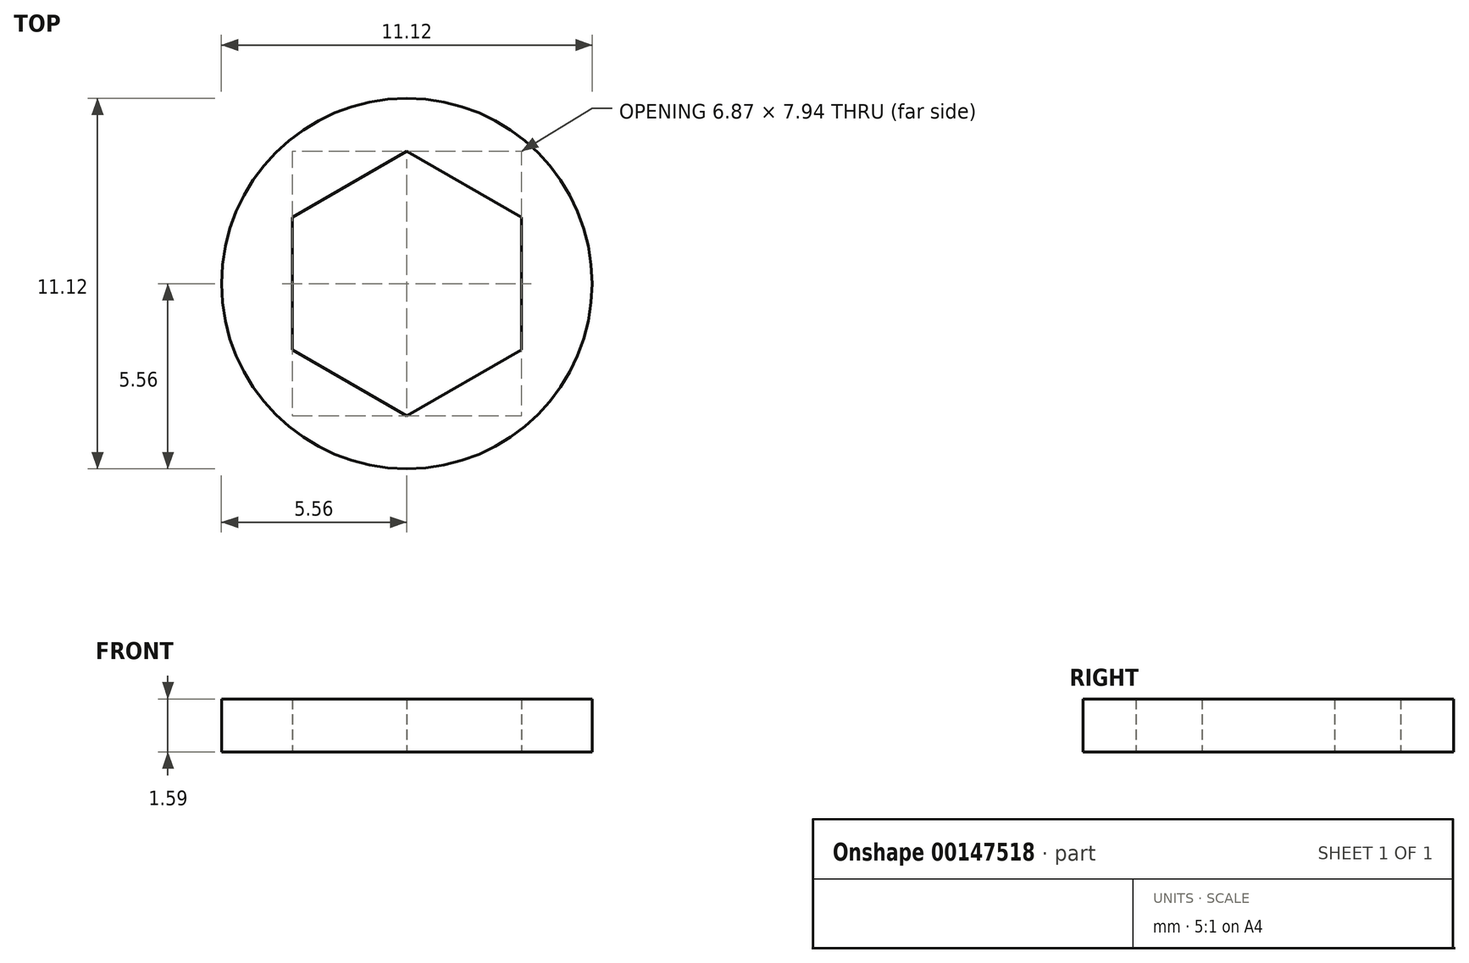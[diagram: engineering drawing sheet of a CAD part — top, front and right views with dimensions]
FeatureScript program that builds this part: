
annotation { "Feature Type Name" : "Feature", "Feature Type Description" : "" }
export const myFeature = defineFeature(function(context is Context, id is Id, definition is map)
    precondition{}
    {
        {
            var Q0;
            Q0=qCreatedBy(makeId("Top.planeOp"),FACE);
            var sketch = newSketch(context, id + "F0", { "sketchPlane" : qUnion([Q0])});
            skCircle(sketch, "E0.cCircle", {"center": v(0, 0) * mm, "radius": 3.97 * mm, "construction": true});
            skLineSegment(sketch, "E0.0", {"start": v(0, -3.97) * mm, "end": v(-3.44, -1.98) * mm});
            skLineSegment(sketch, "E0.1", {"start": v(-3.44, -1.98) * mm, "end": v(-3.44, 1.98) * mm});
            skLineSegment(sketch, "E0.2", {"start": v(-3.44, 1.98) * mm, "end": v(0, 3.97) * mm});
            skLineSegment(sketch, "E0.3", {"start": v(0, 3.97) * mm, "end": v(3.44, 1.98) * mm});
            skLineSegment(sketch, "E0.4", {"start": v(3.44, 1.98) * mm, "end": v(3.44, -1.98) * mm});
            skLineSegment(sketch, "E0.5", {"start": v(3.44, -1.98) * mm, "end": v(0, -3.97) * mm});
            skCircle(sketch, "E1", {"center": v(0, 0) * mm, "radius": 5.56 * mm});
            skSolve(sketch);
        }
        {
            var Q0;
            Q0=qSketchRegion(id+"F0",true);
            extrude(context, id + "F1", {"entities" : qUnion([Q0]), "depth" : 1.59 * mm});
        }
    });
